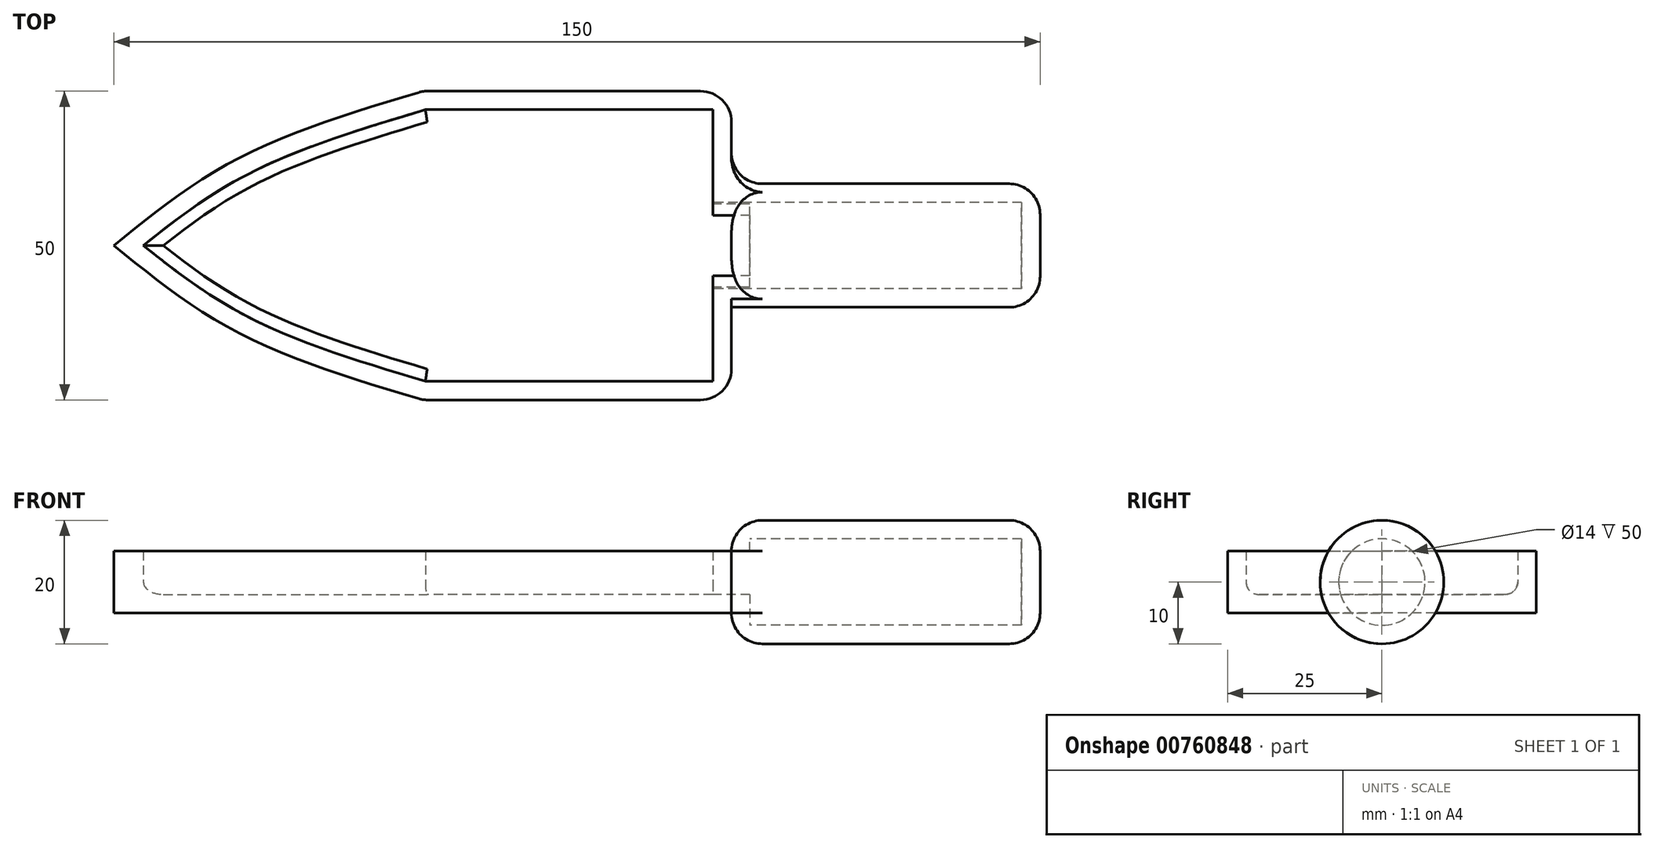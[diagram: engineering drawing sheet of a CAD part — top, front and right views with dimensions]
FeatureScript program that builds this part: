
annotation { "Feature Type Name" : "Feature", "Feature Type Description" : "" }
export const myFeature = defineFeature(function(context is Context, id is Id, definition is map)
    precondition{}
    {
        {
            var Q0;
            Q0=qCreatedBy(makeId("Top.planeOp"),FACE);
            var sketch = newSketch(context, id + "F0", { "sketchPlane" : qUnion([Q0])});
            skLineSegment(sketch, "E0.bottom", {"start": v(50, -25) * mm, "end": v(-50, -25) * mm});
            skLineSegment(sketch, "E0.top", {"start": v(50, 25) * mm, "end": v(-50, 25) * mm});
            skLineSegment(sketch, "E0.left", {"start": v(50, -25) * mm, "end": v(50, 25) * mm});
            skLineSegment(sketch, "E0.right", {"start": v(-50, -25) * mm, "end": v(-50, 25) * mm});
            skPoint(sketch, "E0.middle", {"position": v(0, 0) * mm});
            skFitSpline(sketch, "E1", {"points": [v(0, 25) * mm, v(-29.91, 14.1) * mm, v(-50, 0) * mm], "startDerivative": vector(-59.7, -17.89) * mm, "endDerivative": vector(-39.88, -32.43) * mm});
            skLineSegment(sketch, "E2", {"start": v(-50, 0) * mm, "end": v(50, 0) * mm});
            skFitSpline(sketch, "E3.MirrorCS", {"points": [v(0, -25) * mm, v(-29.91, -14.1) * mm, v(-50, 0) * mm], "startDerivative": vector(-59.7, 17.89) * mm, "endDerivative": vector(-39.88, 32.43) * mm});
            skSolve(sketch);
        }
        {
            var Q0;
            {var subQ4=sQuery(id+"F0.wireOp",EDGE,"E2");Q0=makeQuery(id+"F0.imprint","IMPRINT",FACE,{"disambiguationData":[TD([[makeQuery(id+"F0.imprint","IMPRINT",EDGE,{"derivedFrom":subQ4}),-1.0]])]});}
            var Q1;
            {var subQ3=sQuery(id+"F0.wireOp",EDGE,"E1");Q1=makeQuery(id+"F0.imprint","IMPRINT",FACE,{"disambiguationData":[TD([[makeQuery(id+"F0.imprint","IMPRINT",EDGE,{"derivedFrom":subQ3}),1.0]])]});}
            extrude(context, id + "F1", {"entities" : qUnion([Q0, Q1]), "endBound" : BoundingType.SYMMETRIC, "depth" : 10 * mm, "offsetDistance" : 25 * mm});
        }
        {
            var Q0;
            Q0=makeQuery(id+"F1.opExtrude","SWEPT_FACE",FACE,{"disambiguationData":[OSD([sQuery(id+"F0.wireOp",EDGE,"E0.left")])]});
            var sketch = newSketch(context, id + "F2", { "sketchPlane" : qUnion([Q0])});
            skCircle(sketch, "E4", {"center": v(0, 0) * mm, "radius": 10 * mm});
            skSolve(sketch);
        }
        {
            var Q0;
            Q0 = qSketchRegion(id + "F2", true);
            extrude(context, id + "F3", {"entities" : qUnion([Q0]), "operationType" : NewBodyOperationType.ADD, "depth" : 50 * mm, "offsetDistance" : 25 * mm});
        }
        {
            var Q0;
            Q0=makeQuery(id+"F1.opExtrude","CAP_FACE",FACE,{"disambiguationData":[OSD([sQuery(id+"F0.wireOp",EDGE,"E0.bottom"),sQuery(id+"F0.wireOp",EDGE,"E0.top"),sQuery(id+"F0.wireOp",EDGE,"E0.left"),sQuery(id+"F0.wireOp",EDGE,"E1"),sQuery(id+"F0.wireOp",EDGE,"E3.MirrorCS")])],"isStart":false});
            shell(context, id + "F4", {"entities" : qUnion([Q0]), "thickness" : 3 * mm});
        }
        {
            var Q0;
            Q0=makeQuery(id+"F1.opExtrude","SWEPT_EDGE",EDGE,{"disambiguationData":[OSD([sQuery(id+"F0.wireOp",EDGE,"E0.top"),sQuery(id+"F0.wireOp",EDGE,"E1")])]});
            var Q1;
            Q1=makeQuery(id+"F1.opExtrude","SWEPT_EDGE",EDGE,{"disambiguationData":[OSD([sQuery(id+"F0.wireOp",EDGE,"E0.top"),sQuery(id+"F0.wireOp",EDGE,"E0.left")])]});
            var Q2;
            Q2=makeQuery(id+"F1.opExtrude","SWEPT_EDGE",EDGE,{"disambiguationData":[OSD([sQuery(id+"F0.wireOp",EDGE,"E0.bottom"),sQuery(id+"F0.wireOp",EDGE,"E0.left")])]});
            var Q3;
            Q3=makeQuery(id+"F1.opExtrude","SWEPT_EDGE",EDGE,{"disambiguationData":[OSD([sQuery(id+"F0.wireOp",EDGE,"E0.bottom"),sQuery(id+"F0.wireOp",EDGE,"E3.MirrorCS")])]});
            fillet(context, id + "F5", {"entities" : qUnion([Q0, Q1, Q2, Q3]), "radius" : 5 * mm, "tangentPropagation" : true, "allowEdgeOverflow" : false});
        }
        {
            var Q0;
            Q0=makeQuery(id+"F3.opExtrude","CAP_EDGE",EDGE,{"disambiguationData":[OSD([sQuery(id+"F2.wireOp",EDGE,"E4")])],"isStart":false});
            var Q1;
            {var subQ0=sQuery(id+"F0.wireOp",EDGE,"E0.left");var subQ1=sQuery(id+"F2.wireOp",EDGE,"E4");var subQ2=makeQuery(id+"F3.opExtrude","CAP_FACE",FACE,{"disambiguationData":[OSD([subQ1])],"isStart":true});var subQ3=makeQuery(id+"F3.opExtrude","SWEPT_FACE",FACE,{"disambiguationData":[OSD([subQ1])]});Q1=makeQuery(id+"F3.boolean.opBoolean","SPLIT",EDGE,{"disambiguationData":[topologyDisambiguationEdgeConnected([subQ3,subQ2]),TD([makeQuery(id+"F1.opExtrude","CAP_FACE",FACE,{"disambiguationData":[OSD([sQuery(id+"F0.wireOp",EDGE,"E0.bottom"),sQuery(id+"F0.wireOp",EDGE,"E0.top"),subQ0,sQuery(id+"F0.wireOp",EDGE,"E1"),sQuery(id+"F0.wireOp",EDGE,"E3.MirrorCS")])],"isStart":false})])],"derivedFrom":makeQuery(id+"F3.opExtrude","CAP_EDGE",EDGE,{"disambiguationData":[OSD([subQ1])],"isStart":true})});}
            var Q2;
            {var subQ0=sQuery(id+"F0.wireOp",EDGE,"E0.left");var subQ1=sQuery(id+"F2.wireOp",EDGE,"E4");var subQ2=makeQuery(id+"F3.opExtrude","CAP_FACE",FACE,{"disambiguationData":[OSD([subQ1])],"isStart":true});var subQ3=makeQuery(id+"F3.opExtrude","SWEPT_FACE",FACE,{"disambiguationData":[OSD([subQ1])]});Q2=makeQuery(id+"F3.boolean.opBoolean","SPLIT",EDGE,{"disambiguationData":[topologyDisambiguationEdgeConnected([subQ3,subQ2]),TD([makeQuery(id+"F1.opExtrude","CAP_FACE",FACE,{"disambiguationData":[OSD([sQuery(id+"F0.wireOp",EDGE,"E0.bottom"),sQuery(id+"F0.wireOp",EDGE,"E0.top"),subQ0,sQuery(id+"F0.wireOp",EDGE,"E1"),sQuery(id+"F0.wireOp",EDGE,"E3.MirrorCS")])],"isStart":true})])],"derivedFrom":makeQuery(id+"F3.opExtrude","CAP_EDGE",EDGE,{"disambiguationData":[OSD([subQ1])],"isStart":true})});}
            fillet(context, id + "F6", {"entities" : qUnion([Q0, Q1, Q2]), "radius" : 5 * mm, "tangentPropagation" : true, "allowEdgeOverflow" : false});
        }
        {
            var Q0;
            {var subQ0=sQuery(id+"F2.wireOp",EDGE,"E4");Q0=makeQuery(id+"F3.boolean.opBoolean","SPLIT",EDGE,{"disambiguationData":[topologyDisambiguationEdgeConnected([makeQuery(id+"F1.opExtrude","SWEPT_FACE",FACE,{"disambiguationData":[OSD([sQuery(id+"F0.wireOp",EDGE,"E0.left")])]}),makeQuery(id+"F3.opExtrude","SWEPT_FACE",FACE,{"disambiguationData":[OSD([subQ0])]})]),OD(1.0)],"derivedFrom":makeQuery(id+"F3.opExtrude","CAP_EDGE",EDGE,{"disambiguationData":[OSD([subQ0])],"isStart":true})});}
            var Q1;
            {var subQ0=sQuery(id+"F2.wireOp",EDGE,"E4");Q1=makeQuery(id+"F3.boolean.opBoolean","SPLIT",EDGE,{"disambiguationData":[topologyDisambiguationEdgeConnected([makeQuery(id+"F1.opExtrude","SWEPT_FACE",FACE,{"disambiguationData":[OSD([sQuery(id+"F0.wireOp",EDGE,"E0.left")])]}),makeQuery(id+"F3.opExtrude","SWEPT_FACE",FACE,{"disambiguationData":[OSD([subQ0])]})]),OD(0.0)],"derivedFrom":makeQuery(id+"F3.opExtrude","CAP_EDGE",EDGE,{"disambiguationData":[OSD([subQ0])],"isStart":true})});}
            fillet(context, id + "F7", {"entities" : qUnion([Q0, Q1]), "radius" : 5 * mm, "tangentPropagation" : true, "allowEdgeOverflow" : false});
        }
        {
            var Q0;
            {var subQ0=sQuery(id+"F0.wireOp",EDGE,"E3.MirrorCS");Q0=makeQuery(id+"F4.opShell","OFFSET_EDGE",EDGE,{"disambiguationData":[OSD([subQ0]),TDD([makeQuery(id+"F1.opExtrude","CAP_EDGE",EDGE,{"disambiguationData":[OSD([subQ0])],"isStart":true})])]});}
            var Q1;
            {var subQ0=sQuery(id+"F0.wireOp",EDGE,"E1");Q1=makeQuery(id+"F4.opShell","OFFSET_EDGE",EDGE,{"disambiguationData":[OSD([subQ0]),TDD([makeQuery(id+"F1.opExtrude","CAP_EDGE",EDGE,{"disambiguationData":[OSD([subQ0])],"isStart":true})])]});}
            var Q2;
            {var subQ0=sQuery(id+"F0.wireOp",EDGE,"E0.top");Q2=makeQuery(id+"F4.opShell","OFFSET_EDGE",EDGE,{"disambiguationData":[OSD([subQ0]),TDD([makeQuery(id+"F1.opExtrude","CAP_EDGE",EDGE,{"disambiguationData":[OSD([subQ0])],"isStart":true})])]});}
            var Q3;
            {var subQ0=sQuery(id+"F0.wireOp",EDGE,"E0.bottom");Q3=makeQuery(id+"F4.opShell","OFFSET_EDGE",EDGE,{"disambiguationData":[OSD([subQ0]),TDD([makeQuery(id+"F1.opExtrude","CAP_EDGE",EDGE,{"disambiguationData":[OSD([subQ0])],"isStart":true})])]});}
            fillet(context, id + "F8", {"entities" : qUnion([Q0, Q1, Q2, Q3]), "radius" : 2 * mm, "tangentPropagation" : true, "allowEdgeOverflow" : false});
        }
    });
